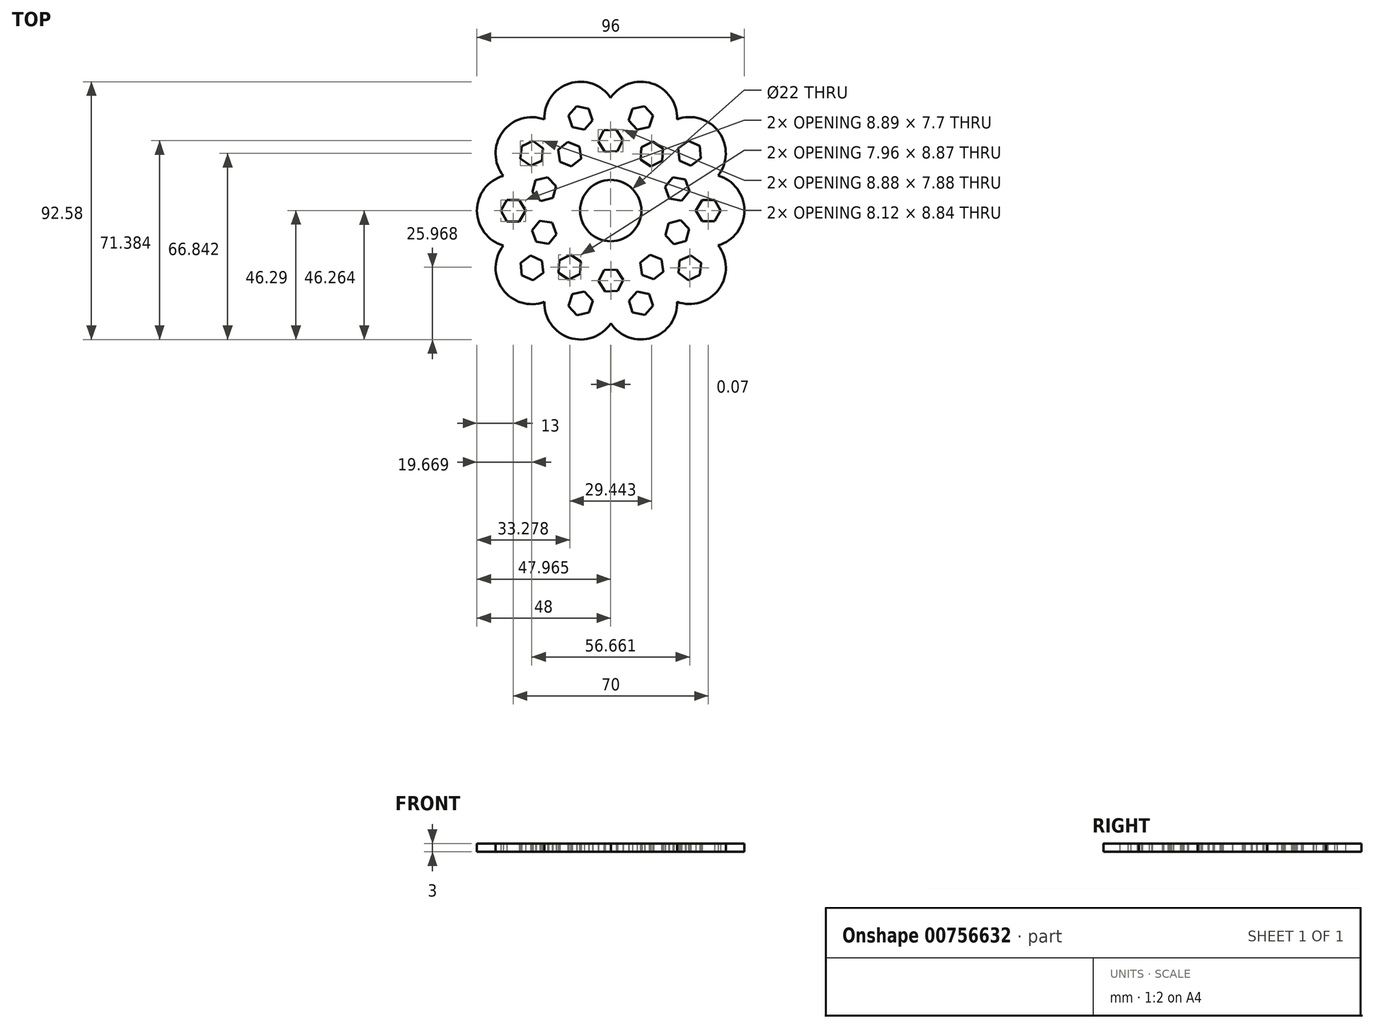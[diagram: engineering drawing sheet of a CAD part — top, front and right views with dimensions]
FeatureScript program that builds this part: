
annotation { "Feature Type Name" : "Feature", "Feature Type Description" : "" }
export const myFeature = defineFeature(function(context is Context, id is Id, definition is map)
    precondition{}
    {
        {
            var Q0;
            Q0=qCreatedBy(makeId("Top.planeOp"),FACE);
            var sketch = newSketch(context, id + "F0", { "sketchPlane" : qUnion([Q0])});
            skCircle(sketch, "E0", {"center": v(0, 0) * mm, "radius": 11 * mm});
            skArc(sketch, "E1", {"start": v(-0.03, 40.5) * mm, "mid": v(-14.87, 45.64) * mm, "end": v(-23.83, 32.75) * mm});
            skArc(sketch, "E2.trimOffspring", {"start": v(-3.64, 22.45) * mm, "mid": v(-3.46, 22.58) * mm, "end": v(-3.28, 22.7) * mm});
            skArc(sketch, "E3.trimOffspring", {"start": v(-10.88, 20.28) * mm, "mid": v(-10.7, 20.28) * mm, "end": v(-10.54, 20.28) * mm});
            skLineSegment(sketch, "E4", {"start": v(-7.43, 35.37) * mm, "end": v(-7.28, 35.43) * mm});
            skArc(sketch, "E5.trimOffspring", {"start": v(-18.2, 22.57) * mm, "mid": v(-18.12, 22.5) * mm, "end": v(-18.02, 22.44) * mm});
            skArc(sketch, "E6.1.0", {"start": v(-23.83, 32.75) * mm, "mid": v(-38.85, 28.19) * mm, "end": v(-38.53, 12.49) * mm});
            skArc(sketch, "E6.2.0", {"start": v(-38.53, 12.49) * mm, "mid": v(-48, -0.04) * mm, "end": v(-38.5, -12.54) * mm});
            skArc(sketch, "E6.3.0", {"start": v(-38.5, -12.54) * mm, "mid": v(-38.81, -28.24) * mm, "end": v(-23.78, -32.78) * mm});
            skArc(sketch, "E6.4.0", {"start": v(-23.78, -32.78) * mm, "mid": v(-14.8, -45.66) * mm, "end": v(0.03, -40.5) * mm});
            skArc(sketch, "E6.5.0", {"start": v(0.03, -40.5) * mm, "mid": v(14.87, -45.64) * mm, "end": v(23.83, -32.75) * mm});
            skArc(sketch, "E6.6.0", {"start": v(23.83, -32.75) * mm, "mid": v(38.85, -28.19) * mm, "end": v(38.53, -12.49) * mm});
            skArc(sketch, "E6.7.0", {"start": v(38.53, -12.49) * mm, "mid": v(48, 0.04) * mm, "end": v(38.5, 12.54) * mm});
            skArc(sketch, "E6.8.0", {"start": v(38.5, 12.54) * mm, "mid": v(38.81, 28.24) * mm, "end": v(23.78, 32.78) * mm});
            skArc(sketch, "E6.9.0", {"start": v(23.78, 32.78) * mm, "mid": v(14.8, 45.66) * mm, "end": v(-0.03, 40.5) * mm});
            skPoint(sketch, "E7.orphan", {"position": v(-36.8, 12.85) * mm});
            skCircle(sketch, "E8.cCircle", {"center": v(23.85, 7.79) * mm, "radius": 3.85 * mm, "construction": true});
            skLineSegment(sketch, "E8.0", {"start": v(28.24, 7.05) * mm, "end": v(25.4, 3.62) * mm});
            skLineSegment(sketch, "E8.1", {"start": v(25.4, 3.62) * mm, "end": v(21.02, 4.36) * mm});
            skLineSegment(sketch, "E8.2", {"start": v(21.02, 4.36) * mm, "end": v(19.47, 8.53) * mm});
            skLineSegment(sketch, "E8.3", {"start": v(19.47, 8.53) * mm, "end": v(22.3, 11.95) * mm});
            skLineSegment(sketch, "E8.4", {"start": v(22.3, 11.95) * mm, "end": v(26.69, 11.21) * mm});
            skLineSegment(sketch, "E8.5", {"start": v(26.69, 11.21) * mm, "end": v(28.24, 7.05) * mm});
            skPoint(sketch, "E8.0.midPoint", {"position": v(26.82, 5.34) * mm});
            skCircle(sketch, "E9.cCircle", {"center": v(35, 0.03) * mm, "radius": 3.85 * mm, "construction": true});
            skLineSegment(sketch, "E9.0", {"start": v(37.23, -3.82) * mm, "end": v(32.78, -3.83) * mm});
            skLineSegment(sketch, "E9.1", {"start": v(32.78, -3.83) * mm, "end": v(30.55, 0.02) * mm});
            skLineSegment(sketch, "E9.2", {"start": v(30.55, 0.02) * mm, "end": v(32.77, 3.87) * mm});
            skLineSegment(sketch, "E9.3", {"start": v(32.77, 3.87) * mm, "end": v(37.22, 3.88) * mm});
            skLineSegment(sketch, "E9.4", {"start": v(37.22, 3.88) * mm, "end": v(39.45, 0.03) * mm});
            skLineSegment(sketch, "E9.5", {"start": v(39.45, 0.03) * mm, "end": v(37.23, -3.82) * mm});
            skPoint(sketch, "E9.0.midPoint", {"position": v(35, -3.82) * mm});
            skPoint(sketch, "E10.1.0", {"position": v(18.56, 20.08) * mm});
            skCircle(sketch, "E10.1.1", {"center": v(14.72, 20.32) * mm, "radius": 3.85 * mm, "construction": true});
            skLineSegment(sketch, "E10.1.2", {"start": v(10.74, 18.34) * mm, "end": v(11.02, 22.78) * mm});
            skLineSegment(sketch, "E10.1.3", {"start": v(14.45, 15.88) * mm, "end": v(10.74, 18.34) * mm});
            skLineSegment(sketch, "E10.1.4", {"start": v(11.02, 22.78) * mm, "end": v(15, 24.76) * mm});
            skLineSegment(sketch, "E10.1.5", {"start": v(15, 24.76) * mm, "end": v(18.7, 22.3) * mm});
            skLineSegment(sketch, "E10.1.6", {"start": v(18.7, 22.3) * mm, "end": v(18.43, 17.86) * mm});
            skLineSegment(sketch, "E10.1.7", {"start": v(18.43, 17.86) * mm, "end": v(14.45, 15.88) * mm});
            skPoint(sketch, "E10.2.0", {"position": v(3.21, 27.16) * mm});
            skCircle(sketch, "E10.2.1", {"center": v(-0.03, 25.1) * mm, "radius": 3.85 * mm, "construction": true});
            skLineSegment(sketch, "E10.2.2", {"start": v(-2.1, 21.15) * mm, "end": v(-4.48, 24.9) * mm});
            skLineSegment(sketch, "E10.2.3", {"start": v(2.35, 21.34) * mm, "end": v(-2.1, 21.15) * mm});
            skLineSegment(sketch, "E10.2.4", {"start": v(-4.48, 24.9) * mm, "end": v(-2.42, 28.85) * mm});
            skLineSegment(sketch, "E10.2.5", {"start": v(-2.42, 28.85) * mm, "end": v(2.02, 29.04) * mm});
            skLineSegment(sketch, "E10.2.6", {"start": v(2.02, 29.04) * mm, "end": v(4.4, 25.28) * mm});
            skLineSegment(sketch, "E10.2.7", {"start": v(4.4, 25.28) * mm, "end": v(2.35, 21.34) * mm});
            skPoint(sketch, "E10.3.0", {"position": v(-13.36, 23.86) * mm});
            skCircle(sketch, "E10.3.1", {"center": v(-14.78, 20.28) * mm, "radius": 3.85 * mm, "construction": true});
            skLineSegment(sketch, "E10.3.2", {"start": v(-14.13, 15.88) * mm, "end": v(-18.26, 17.52) * mm});
            skLineSegment(sketch, "E10.3.3", {"start": v(-10.64, 18.65) * mm, "end": v(-14.13, 15.88) * mm});
            skLineSegment(sketch, "E10.3.4", {"start": v(-18.26, 17.52) * mm, "end": v(-18.91, 21.91) * mm});
            skLineSegment(sketch, "E10.3.5", {"start": v(-18.91, 21.91) * mm, "end": v(-15.43, 24.68) * mm});
            skLineSegment(sketch, "E10.3.6", {"start": v(-15.43, 24.68) * mm, "end": v(-11.3, 23.04) * mm});
            skLineSegment(sketch, "E10.3.7", {"start": v(-11.3, 23.04) * mm, "end": v(-10.64, 18.65) * mm});
            skPoint(sketch, "E10.4.0", {"position": v(-24.84, 11.45) * mm});
            skCircle(sketch, "E10.4.1", {"center": v(-23.88, 7.72) * mm, "radius": 3.85 * mm, "construction": true});
            skLineSegment(sketch, "E10.4.2", {"start": v(-20.76, 4.55) * mm, "end": v(-25.07, 3.44) * mm});
            skLineSegment(sketch, "E10.4.3", {"start": v(-19.57, 8.83) * mm, "end": v(-20.76, 4.55) * mm});
            skLineSegment(sketch, "E10.4.4", {"start": v(-25.07, 3.44) * mm, "end": v(-28.18, 6.61) * mm});
            skLineSegment(sketch, "E10.4.5", {"start": v(-28.18, 6.61) * mm, "end": v(-26.99, 10.9) * mm});
            skLineSegment(sketch, "E10.4.6", {"start": v(-26.99, 10.9) * mm, "end": v(-22.68, 12) * mm});
            skLineSegment(sketch, "E10.4.7", {"start": v(-22.68, 12) * mm, "end": v(-19.57, 8.83) * mm});
            skPoint(sketch, "E10.5.0", {"position": v(-26.82, -5.34) * mm});
            skCircle(sketch, "E10.5.1", {"center": v(-23.85, -7.79) * mm, "radius": 3.85 * mm, "construction": true});
            skLineSegment(sketch, "E10.5.2", {"start": v(-19.47, -8.53) * mm, "end": v(-22.3, -11.95) * mm});
            skLineSegment(sketch, "E10.5.3", {"start": v(-21.02, -4.36) * mm, "end": v(-19.47, -8.53) * mm});
            skLineSegment(sketch, "E10.5.4", {"start": v(-22.3, -11.95) * mm, "end": v(-26.69, -11.21) * mm});
            skLineSegment(sketch, "E10.5.5", {"start": v(-26.69, -11.21) * mm, "end": v(-28.24, -7.05) * mm});
            skLineSegment(sketch, "E10.5.6", {"start": v(-28.24, -7.05) * mm, "end": v(-25.4, -3.62) * mm});
            skLineSegment(sketch, "E10.5.7", {"start": v(-25.4, -3.62) * mm, "end": v(-21.02, -4.36) * mm});
            skPoint(sketch, "E10.6.0", {"position": v(-18.56, -20.08) * mm});
            skCircle(sketch, "E10.6.1", {"center": v(-14.72, -20.32) * mm, "radius": 3.85 * mm, "construction": true});
            skLineSegment(sketch, "E10.6.2", {"start": v(-10.74, -18.34) * mm, "end": v(-11.02, -22.78) * mm});
            skLineSegment(sketch, "E10.6.3", {"start": v(-14.45, -15.88) * mm, "end": v(-10.74, -18.34) * mm});
            skLineSegment(sketch, "E10.6.4", {"start": v(-11.02, -22.78) * mm, "end": v(-15, -24.76) * mm});
            skLineSegment(sketch, "E10.6.5", {"start": v(-15, -24.76) * mm, "end": v(-18.7, -22.3) * mm});
            skLineSegment(sketch, "E10.6.6", {"start": v(-18.7, -22.3) * mm, "end": v(-18.43, -17.86) * mm});
            skLineSegment(sketch, "E10.6.7", {"start": v(-18.43, -17.86) * mm, "end": v(-14.45, -15.88) * mm});
            skPoint(sketch, "E10.7.0", {"position": v(-3.21, -27.16) * mm});
            skCircle(sketch, "E10.7.1", {"center": v(0.03, -25.1) * mm, "radius": 3.85 * mm, "construction": true});
            skLineSegment(sketch, "E10.7.2", {"start": v(2.1, -21.15) * mm, "end": v(4.48, -24.9) * mm});
            skLineSegment(sketch, "E10.7.3", {"start": v(-2.35, -21.34) * mm, "end": v(2.1, -21.15) * mm});
            skLineSegment(sketch, "E10.7.4", {"start": v(4.48, -24.9) * mm, "end": v(2.42, -28.85) * mm});
            skLineSegment(sketch, "E10.7.5", {"start": v(2.42, -28.85) * mm, "end": v(-2.02, -29.04) * mm});
            skLineSegment(sketch, "E10.7.6", {"start": v(-2.02, -29.04) * mm, "end": v(-4.4, -25.28) * mm});
            skLineSegment(sketch, "E10.7.7", {"start": v(-4.4, -25.28) * mm, "end": v(-2.35, -21.34) * mm});
            skPoint(sketch, "E10.8.0", {"position": v(13.36, -23.86) * mm});
            skCircle(sketch, "E10.8.1", {"center": v(14.78, -20.28) * mm, "radius": 3.85 * mm, "construction": true});
            skLineSegment(sketch, "E10.8.2", {"start": v(14.13, -15.88) * mm, "end": v(18.26, -17.52) * mm});
            skLineSegment(sketch, "E10.8.3", {"start": v(10.64, -18.65) * mm, "end": v(14.13, -15.88) * mm});
            skLineSegment(sketch, "E10.8.4", {"start": v(18.26, -17.52) * mm, "end": v(18.91, -21.91) * mm});
            skLineSegment(sketch, "E10.8.5", {"start": v(18.91, -21.91) * mm, "end": v(15.43, -24.68) * mm});
            skLineSegment(sketch, "E10.8.6", {"start": v(15.43, -24.68) * mm, "end": v(11.3, -23.04) * mm});
            skLineSegment(sketch, "E10.8.7", {"start": v(11.3, -23.04) * mm, "end": v(10.64, -18.65) * mm});
            skPoint(sketch, "E10.9.0", {"position": v(24.84, -11.45) * mm});
            skCircle(sketch, "E10.9.1", {"center": v(23.88, -7.72) * mm, "radius": 3.85 * mm, "construction": true});
            skLineSegment(sketch, "E10.9.2", {"start": v(20.76, -4.55) * mm, "end": v(25.07, -3.44) * mm});
            skLineSegment(sketch, "E10.9.3", {"start": v(19.57, -8.83) * mm, "end": v(20.76, -4.55) * mm});
            skLineSegment(sketch, "E10.9.4", {"start": v(25.07, -3.44) * mm, "end": v(28.18, -6.61) * mm});
            skLineSegment(sketch, "E10.9.5", {"start": v(28.18, -6.61) * mm, "end": v(26.99, -10.9) * mm});
            skLineSegment(sketch, "E10.9.6", {"start": v(26.99, -10.9) * mm, "end": v(22.68, -12) * mm});
            skLineSegment(sketch, "E10.9.7", {"start": v(22.68, -12) * mm, "end": v(19.57, -8.83) * mm});
            skLineSegment(sketch, "E11.1.0", {"start": v(24.24, 22.4) * mm, "end": v(27.83, 25.01) * mm});
            skLineSegment(sketch, "E11.1.1", {"start": v(24.7, 17.98) * mm, "end": v(24.24, 22.4) * mm});
            skLineSegment(sketch, "E11.1.2", {"start": v(27.83, 25.01) * mm, "end": v(31.9, 23.2) * mm});
            skLineSegment(sketch, "E11.1.3", {"start": v(31.9, 23.2) * mm, "end": v(32.36, 18.79) * mm});
            skLineSegment(sketch, "E11.1.4", {"start": v(28.77, 16.17) * mm, "end": v(24.7, 17.98) * mm});
            skCircle(sketch, "E11.1.5", {"center": v(28.3, 20.6) * mm, "radius": 3.85 * mm, "construction": true});
            skLineSegment(sketch, "E11.1.6", {"start": v(32.36, 18.79) * mm, "end": v(28.77, 16.17) * mm});
            skLineSegment(sketch, "E11.2.0", {"start": v(6.44, 32.37) * mm, "end": v(7.81, 36.6) * mm});
            skLineSegment(sketch, "E11.2.1", {"start": v(9.42, 29.07) * mm, "end": v(6.44, 32.37) * mm});
            skLineSegment(sketch, "E11.2.2", {"start": v(7.81, 36.6) * mm, "end": v(12.16, 37.52) * mm});
            skLineSegment(sketch, "E11.2.3", {"start": v(12.16, 37.52) * mm, "end": v(15.14, 34.22) * mm});
            skLineSegment(sketch, "E11.2.4", {"start": v(13.77, 30) * mm, "end": v(9.42, 29.07) * mm});
            skCircle(sketch, "E11.2.5", {"center": v(10.8, 33.3) * mm, "radius": 3.85 * mm, "construction": true});
            skLineSegment(sketch, "E11.2.6", {"start": v(15.14, 34.22) * mm, "end": v(13.77, 30) * mm});
            skLineSegment(sketch, "E11.3.0", {"start": v(-13.81, 29.97) * mm, "end": v(-15.19, 34.2) * mm});
            skLineSegment(sketch, "E11.3.1", {"start": v(-9.46, 29.05) * mm, "end": v(-13.81, 29.97) * mm});
            skLineSegment(sketch, "E11.3.2", {"start": v(-15.19, 34.2) * mm, "end": v(-12.22, 37.5) * mm});
            skLineSegment(sketch, "E11.3.3", {"start": v(-12.22, 37.5) * mm, "end": v(-7.87, 36.58) * mm});
            skLineSegment(sketch, "E11.3.4", {"start": v(-6.5, 32.36) * mm, "end": v(-9.46, 29.05) * mm});
            skCircle(sketch, "E11.3.5", {"center": v(-10.84, 33.28) * mm, "radius": 3.85 * mm, "construction": true});
            skLineSegment(sketch, "E11.3.6", {"start": v(-7.87, 36.58) * mm, "end": v(-6.5, 32.36) * mm});
            skLineSegment(sketch, "E11.4.0", {"start": v(-28.8, 16.13) * mm, "end": v(-32.4, 18.74) * mm});
            skLineSegment(sketch, "E11.4.1", {"start": v(-24.73, 17.94) * mm, "end": v(-28.8, 16.13) * mm});
            skLineSegment(sketch, "E11.4.2", {"start": v(-32.4, 18.74) * mm, "end": v(-31.93, 23.16) * mm});
            skLineSegment(sketch, "E11.4.3", {"start": v(-31.93, 23.16) * mm, "end": v(-27.87, 24.97) * mm});
            skLineSegment(sketch, "E11.4.4", {"start": v(-24.27, 22.36) * mm, "end": v(-24.73, 17.94) * mm});
            skCircle(sketch, "E11.4.5", {"center": v(-28.33, 20.55) * mm, "radius": 3.85 * mm, "construction": true});
            skLineSegment(sketch, "E11.4.6", {"start": v(-27.87, 24.97) * mm, "end": v(-24.27, 22.36) * mm});
            skLineSegment(sketch, "E11.5.0", {"start": v(-32.77, -3.87) * mm, "end": v(-37.22, -3.88) * mm});
            skLineSegment(sketch, "E11.5.1", {"start": v(-30.55, -0.02) * mm, "end": v(-32.77, -3.87) * mm});
            skLineSegment(sketch, "E11.5.2", {"start": v(-37.22, -3.88) * mm, "end": v(-39.45, -0.03) * mm});
            skLineSegment(sketch, "E11.5.3", {"start": v(-39.45, -0.03) * mm, "end": v(-37.23, 3.82) * mm});
            skLineSegment(sketch, "E11.5.4", {"start": v(-32.78, 3.83) * mm, "end": v(-30.55, -0.02) * mm});
            skCircle(sketch, "E11.5.5", {"center": v(-35, -0.03) * mm, "radius": 3.85 * mm, "construction": true});
            skLineSegment(sketch, "E11.5.6", {"start": v(-37.23, 3.82) * mm, "end": v(-32.78, 3.83) * mm});
            skLineSegment(sketch, "E11.6.0", {"start": v(-24.24, -22.4) * mm, "end": v(-27.83, -25.01) * mm});
            skLineSegment(sketch, "E11.6.1", {"start": v(-24.7, -17.98) * mm, "end": v(-24.24, -22.4) * mm});
            skLineSegment(sketch, "E11.6.2", {"start": v(-27.83, -25.01) * mm, "end": v(-31.9, -23.2) * mm});
            skLineSegment(sketch, "E11.6.3", {"start": v(-31.9, -23.2) * mm, "end": v(-32.36, -18.79) * mm});
            skLineSegment(sketch, "E11.6.4", {"start": v(-28.77, -16.17) * mm, "end": v(-24.7, -17.98) * mm});
            skCircle(sketch, "E11.6.5", {"center": v(-28.3, -20.6) * mm, "radius": 3.85 * mm, "construction": true});
            skLineSegment(sketch, "E11.6.6", {"start": v(-32.36, -18.79) * mm, "end": v(-28.77, -16.17) * mm});
            skLineSegment(sketch, "E11.7.0", {"start": v(-6.44, -32.37) * mm, "end": v(-7.81, -36.6) * mm});
            skLineSegment(sketch, "E11.7.1", {"start": v(-9.42, -29.07) * mm, "end": v(-6.44, -32.37) * mm});
            skLineSegment(sketch, "E11.7.2", {"start": v(-7.81, -36.6) * mm, "end": v(-12.16, -37.52) * mm});
            skLineSegment(sketch, "E11.7.3", {"start": v(-12.16, -37.52) * mm, "end": v(-15.14, -34.22) * mm});
            skLineSegment(sketch, "E11.7.4", {"start": v(-13.77, -30) * mm, "end": v(-9.42, -29.07) * mm});
            skCircle(sketch, "E11.7.5", {"center": v(-10.8, -33.3) * mm, "radius": 3.85 * mm, "construction": true});
            skLineSegment(sketch, "E11.7.6", {"start": v(-15.14, -34.22) * mm, "end": v(-13.77, -30) * mm});
            skLineSegment(sketch, "E11.8.0", {"start": v(13.81, -29.97) * mm, "end": v(15.19, -34.2) * mm});
            skLineSegment(sketch, "E11.8.1", {"start": v(9.46, -29.05) * mm, "end": v(13.81, -29.97) * mm});
            skLineSegment(sketch, "E11.8.2", {"start": v(15.19, -34.2) * mm, "end": v(12.22, -37.5) * mm});
            skLineSegment(sketch, "E11.8.3", {"start": v(12.22, -37.5) * mm, "end": v(7.87, -36.58) * mm});
            skLineSegment(sketch, "E11.8.4", {"start": v(6.5, -32.36) * mm, "end": v(9.46, -29.05) * mm});
            skCircle(sketch, "E11.8.5", {"center": v(10.84, -33.28) * mm, "radius": 3.85 * mm, "construction": true});
            skLineSegment(sketch, "E11.8.6", {"start": v(7.87, -36.58) * mm, "end": v(6.5, -32.36) * mm});
            skLineSegment(sketch, "E11.9.0", {"start": v(28.8, -16.13) * mm, "end": v(32.4, -18.74) * mm});
            skLineSegment(sketch, "E11.9.1", {"start": v(24.73, -17.94) * mm, "end": v(28.8, -16.13) * mm});
            skLineSegment(sketch, "E11.9.2", {"start": v(32.4, -18.74) * mm, "end": v(31.93, -23.16) * mm});
            skLineSegment(sketch, "E11.9.3", {"start": v(31.93, -23.16) * mm, "end": v(27.87, -24.97) * mm});
            skLineSegment(sketch, "E11.9.4", {"start": v(24.27, -22.36) * mm, "end": v(24.73, -17.94) * mm});
            skCircle(sketch, "E11.9.5", {"center": v(28.33, -20.55) * mm, "radius": 3.85 * mm, "construction": true});
            skLineSegment(sketch, "E11.9.6", {"start": v(27.87, -24.97) * mm, "end": v(24.27, -22.36) * mm});
            skSolve(sketch);
        }
        {
            var Q0;
            Q0 = qSketchRegion(id + "F0", true);
            extrude(context, id + "F1", {"entities" : qUnion([Q0]), "depth" : 3 * mm, "offsetDistance" : 25 * mm});
        }
    });
